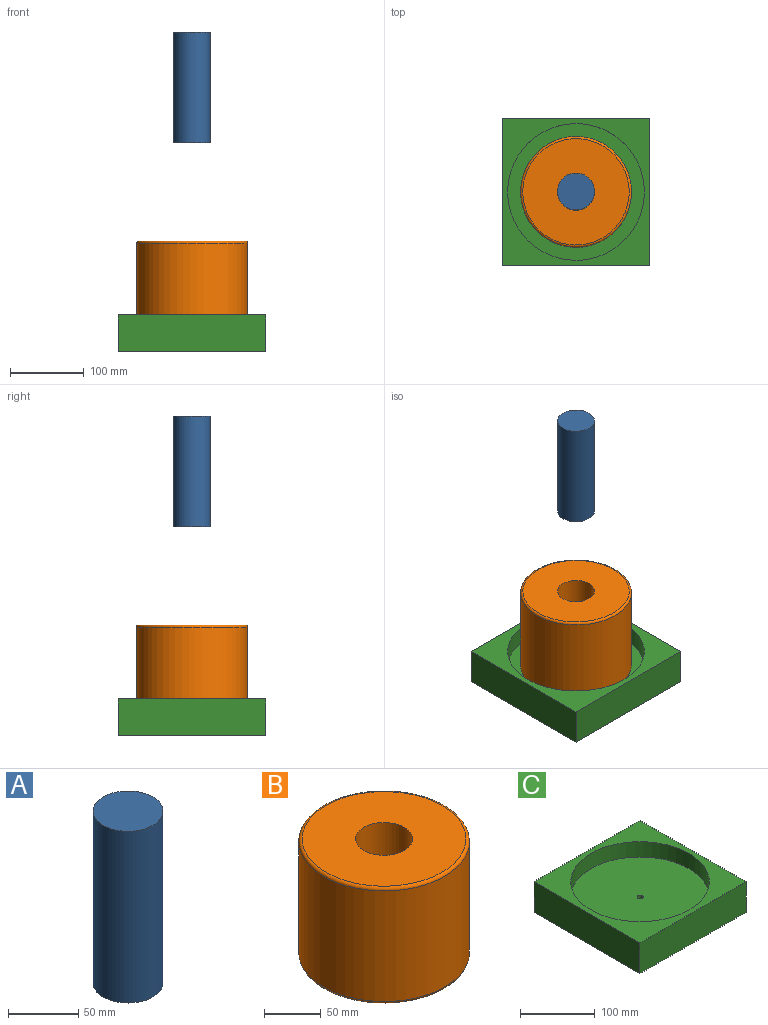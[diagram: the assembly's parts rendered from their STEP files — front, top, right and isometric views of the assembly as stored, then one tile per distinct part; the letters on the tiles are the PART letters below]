
ASSEMBLY  parts=3 mates=2
PART A: 3 faces, bbox 50x50x150 mm
  f0: cylinder r=24.98mm len=150mm, axis (0,0,-1), area 23538.4mm2, adj f1,f2
  f1: plane 49.95x49.95mm, normal (0,0,1), area 1959.6mm2, adj f0
  f2: plane 49.95x49.95mm, normal (0,0,-1), area 1959.6mm2, adj f0
PART B: 6 faces, bbox 162.4x162.4x125 mm
  f0: cylinder r=75mm len=150mm, axis (0,0,-1), area 56077.4mm2, adj f3,f4
  f1: plane 144x144mm, normal (0,0,1), area 14322.5mm2, adj f4,f5
  f2: plane 144x144mm, normal (0,0,-1), area 14322.5mm2, adj f3,f5
  f3: torus R=72mm, axis (0,0,1), area 2188.4mm2, adj f0,f2
  f4: torus R=72mm, axis (0,0,1), area 2188.4mm2, adj f0,f1
  f5: cylinder r=25mm len=125mm, axis (0,0,1), area 19635mm2, adj f1,f2
PART C: 9 faces, bbox 200x200x50 mm
  f0: plane 200x50mm, normal (0,1,0), area 10000mm2, adj f1,f3,f4,f5
  f1: plane 200x50mm, normal (-1,0,0), area 10000mm2, adj f0,f2,f4,f5
  f2: plane 200x50mm, normal (0,-1,0), area 10000mm2, adj f1,f3,f4,f5
  f3: plane 200x50mm, normal (1,0,0), area 10000mm2, adj f0,f2,f4,f5
  f4: plane 200x200mm, normal (0,0,1), area 13119.7mm2, adj f0,f1,f2,f3,f6
  f5: plane 200x200mm, normal (0,0,-1), area 39946.5mm2, adj f0,f1,f2,f3,f8
  f6: cylinder r=92.5mm len=185mm, axis (0,0,1), area 14529.9mm2, adj f4,f7
  f7: plane 185x185mm, normal (0,0,1), area 26826.8mm2, adj f6,f8
  f8: cylinder r=4.12mm len=25mm, axis (0,0,1), area 648mm2, adj f5,f7
PLACE A t=(0,0,282.62)mm
PLACE B t=(0,0,25)mm
PLACE C at identity fixed
MATE fastened C.f6 <-> B.f0  axis (0,0,1) through (0,0,25)mm
MATE slider B.f5 <-> A.f0  axis (0,0,1) through (0,0,150)mm
